# Revit family: КА РАШВОРК  арт.505 .rfa
name_source: partatom
category: Арматура трубопроводов
units: mm (PartAtom-declared; Revit-internal decimal feet)

## family parameters
Всегда вертикально = Нет
На основе рабочей плоскости = Нет
Общий = Нет
При загрузке вырезать с полостями = Да
Размер круглого соединителя = Использовать диаметр
Тип детали = Вставляется

## types (8) — shared parameters
ADSK_Единица измерения = шт
ADSK_Завод-изготовитель = ООО "ТД "РАШВОРК"
URL = https://rwru.ru
Изготовитель = ООО "ТД "РАШВОРК"
Корпус = EPDM
Муфтовое соединение = Ковкий чугун
Уго_длинна = 115 мм
zero-valued in all types: Отметка по умолчанию

## per-type parameters (varying)
| type | ADSK_Код изделия | ADSK_Масса | DN | DN_соединителя | L | L2 | LL | LL2 | LL3 | LL_2 | LL_3 | Корпус_ |
| Компенсатор антивибрационный РАШВОРК 505-015-16, DN015, PN16, корпус - EPDM+Nylon, резьбовое соединение - ковкий чугун, ВР/ВР | 505-015-16 | 0.71 | 15 мм | 15 мм | 200 мм | 100 мм | 30 мм | 57 мм | 17 мм | 51 мм | 25 мм | Корпус : Корпус15 |
| Компенсатор антивибрационный РАШВОРК 505-080-16, DN080, PN16, корпус - EPDM+Nylon, резьбовое соединение - ковкий чугун, ВР/ВР | 505-080-16 | 5.78 | 80 мм | 80 мм | 240 мм | 120 мм | 96 мм | 84 мм | 34 мм | 114 мм | 34 мм | Корпус : Корпус80 |
| Компенсатор антивибрационный РАШВОРК 505-065-16, DN065, PN16, корпус - EPDM+Nylon, резьбовое соединение - ковкий чугун, ВР/ВР | 505-065-16 | 3.8 | 65 мм | 65 мм | 240 мм | 120 мм | 82 мм | 84 мм | 36 мм | 114 мм | 34 мм | Корпус : Корпус65 |
| Компенсатор антивибрационный РАШВОРК 505-040-16, DN040, PN16, корпус - EPDM+Nylon, резьбовое соединение - ковкий чугун, ВР/ВР | 505-040-16 | 2.1 | 40 мм | 40 мм | 200 мм | 100 мм | 56 мм | 64 мм | 24 мм | 79 мм | 27 мм | Корпус : Корпус40 |
| Компенсатор антивибрационный РАШВОРК 505-050-16, DN050, PN16, корпус - EPDM+Nylon, резьбовое соединение - ковкий чугун, ВР/ВР | 505-050-16 | 2.71 | 50 мм | 50 мм | 200 мм | 100 мм | 68 мм | 70 мм | 30 мм | 95 мм | 29 мм | Корпус : Корпус50 |
| Компенсатор антивибрационный РАШВОРК 505-032-16, DN032, PN16, корпус - EPDM+Nylon, резьбовое соединение - ковкий чугун, ВР/ВР | 505-032-16 | 1.51 | 32 мм | 32 мм | 200 мм | 100 мм | 50 мм | 65 мм | 20 мм | 72 мм | 26 мм | Корпус : Корпус32 |
| Компенсатор антивибрационный РАШВОРК 505-025-16, DN025, PN16, корпус - EPDM+Nylon, резьбовое соединение - ковкий чугун, ВР/ВР | 505-025-16 | 1.23 | 25 мм | 25 мм | 200 мм | 100 мм | 42 мм | 63 мм | 20 мм | 64 мм | 25 мм | Корпус : Корпус25 |
| Компенсатор антивибрационный РАШВОРК 505-020-16, DN020, PN16, корпус - EPDM+Nylon, резьбовое соединение - ковкий чугун, ВР/ВР | 505-020-16 | 0.71 | 20 мм | 20 мм | 200 мм | 100 мм | 33 мм | 52 мм | 15 мм | 51 мм | 22 мм | Корпус : Корпус20 |

note: column(s) folded — value = type name in every type: ADSK_Наименование

## geometry (parser evidence)
native form markers: Blend x2
no freeform markers — native parametric forms only
